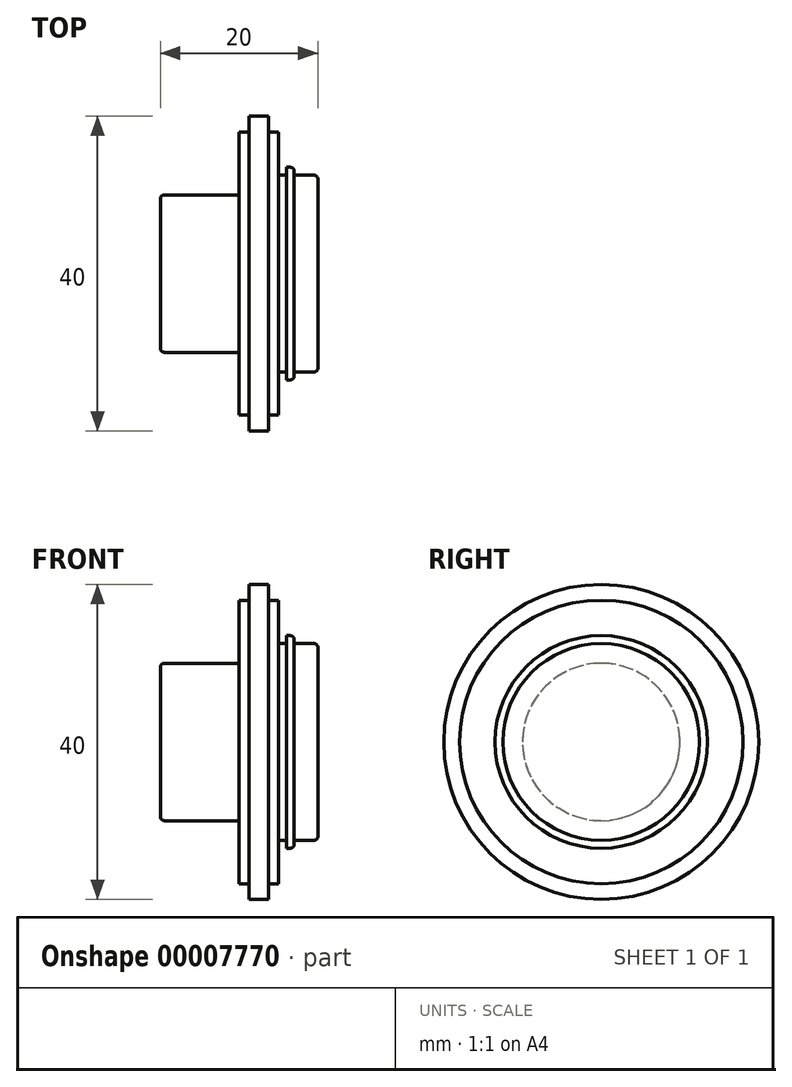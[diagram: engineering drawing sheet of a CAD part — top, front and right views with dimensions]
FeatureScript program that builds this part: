
annotation { "Feature Type Name" : "Feature", "Feature Type Description" : "" }
export const myFeature = defineFeature(function(context is Context, id is Id, definition is map)
    precondition{}
    {
        {
            var Q0;
            Q0=qCreatedBy(makeId("Front.planeOp"),FACE);
            var sketch = newSketch(context, id + "F0", { "sketchPlane" : qUnion([Q0])});
            skLineSegment(sketch, "E0.bottom", {"start": v(-20, 0) * mm, "end": v(0, 0) * mm});
            skLineSegment(sketch, "E0.top", {"start": v(-10, 18) * mm, "end": v(-8.75, 18) * mm});
            skLineSegment(sketch, "E0.right", {"start": v(-5, 12.5) * mm, "end": v(-5, 18) * mm});
            skLineSegment(sketch, "E1.rect.bottom", {"start": v(-6.25, 20) * mm, "end": v(-8.75, 20) * mm});
            skLineSegment(sketch, "E1.rect.left", {"start": v(-6.25, 20) * mm, "end": v(-6.25, 18) * mm});
            skLineSegment(sketch, "E1.rect.right", {"start": v(-8.75, 20) * mm, "end": v(-8.75, 18) * mm});
            skLineSegment(sketch, "E2.trimOffspring", {"start": v(-6.25, 18) * mm, "end": v(-5, 18) * mm});
            skLineSegment(sketch, "E3.bottom", {"start": v(-10, 10) * mm, "end": v(-20, 10) * mm});
            skLineSegment(sketch, "E3.right", {"start": v(-20, 10) * mm, "end": v(-20, 0) * mm});
            skLineSegment(sketch, "E4.trimOffspring", {"start": v(-10, 10) * mm, "end": v(-10, 18) * mm});
            skLineSegment(sketch, "E5", {"start": v(-5, 12.5) * mm, "end": v(-4, 12.5) * mm});
            skLineSegment(sketch, "E6", {"start": v(0, 12.5) * mm, "end": v(0, 0) * mm});
            skLineSegment(sketch, "E7.bottom", {"start": v(-4, 13.5) * mm, "end": v(-3, 13.5) * mm});
            skLineSegment(sketch, "E7.left", {"start": v(-4, 13.5) * mm, "end": v(-4, 12.5) * mm});
            skLineSegment(sketch, "E7.right", {"start": v(-3, 13.5) * mm, "end": v(-3, 12.5) * mm});
            skLineSegment(sketch, "E8.trimOffspring", {"start": v(-3, 12.5) * mm, "end": v(0, 12.5) * mm});
            skSolve(sketch);
        }
        {
            var Q0;
            Q0 = qSketchRegion(id + "F0", true);
            var Q1;
            Q1=sQuery(id+"F0.wireOp",EDGE,"E0.bottom");
            revolve(context, id + "F1", {"entities" : qUnion([Q0]), "axis" : qUnion([Q1]), "revolveType" : RevolveType.FULL});
        }
        {
            var Q0;
            Q0=makeQuery(id+"F1.opRevolve","SWEPT_EDGE",EDGE,{"disambiguationData":[OSD([sQuery(id+"F0.wireOp",EDGE,"E6"),sQuery(id+"F0.wireOp",EDGE,"E8.trimOffspring")])]});
            var Q1;
            Q1=makeQuery(id+"F1.opRevolve","SWEPT_EDGE",EDGE,{"disambiguationData":[OSD([sQuery(id+"F0.wireOp",EDGE,"E7.bottom"),sQuery(id+"F0.wireOp",EDGE,"E7.right")])]});
            var Q2;
            Q2=makeQuery(id+"F1.opRevolve","SWEPT_EDGE",EDGE,{"disambiguationData":[OSD([sQuery(id+"F0.wireOp",EDGE,"E3.bottom"),sQuery(id+"F0.wireOp",EDGE,"E3.right")])]});
            fillet(context, id + "F2", {"entities" : qUnion([Q0, Q1, Q2]), "radius" : 0.5 * mm, "allowEdgeOverflow" : false});
        }
    });
